# Revit family: Urinal-Wall-Caroma H2Zero Cube Waterless
name_source: partatom
category: Plumbing Fixtures
revit_build: Autodesk Revit 2014 (Build: 20131024_2115(x64)
units: mm (PartAtom-declared; Revit-internal decimal feet)

## types (1)
- Standard
    Assembly Code = C1030210
    CW Connection = Yes
    CWFU = 1
    Cost = 0 $
    Default Elevation = 610 mm  [stored 2.00131 ft]
    Description = Caroma H2Zero Cube Waterless Urinal
    HW Connection = No
    Hardware = Metal-Chrome-Caroma
    Height_ANZRS = 600 mm
    Keynote = UR
    Length_ANZRS = 260 mm  [stored 0.853018 ft]
    Manufacturer = GWA Bathrooms & Kitchens
    Material_ANZRS = Porcelain-White-Caroma
    Model = 678610W
    ModifiedIssue_ANZRS = 20140917.01 $
    Type Comments = Optional Vitreous China dome available for light commercial applications
    URL = http://www.caroma.com.au
    Vent Connection = No
    WELSRating_ANZRS = WELS 7 Star rated, 0L
    WFU = 0
    Waste Connection = Yes
    Width_ANZRS = 333 mm  [stored 1.09252 ft]

note: [stored X ft] marks values corroborated as IEEE doubles in the binary element streams (Revit-internal decimal feet)

## geometry (parser evidence)
native form markers: Blend x16, Sweep x1
no freeform markers — native parametric forms only
